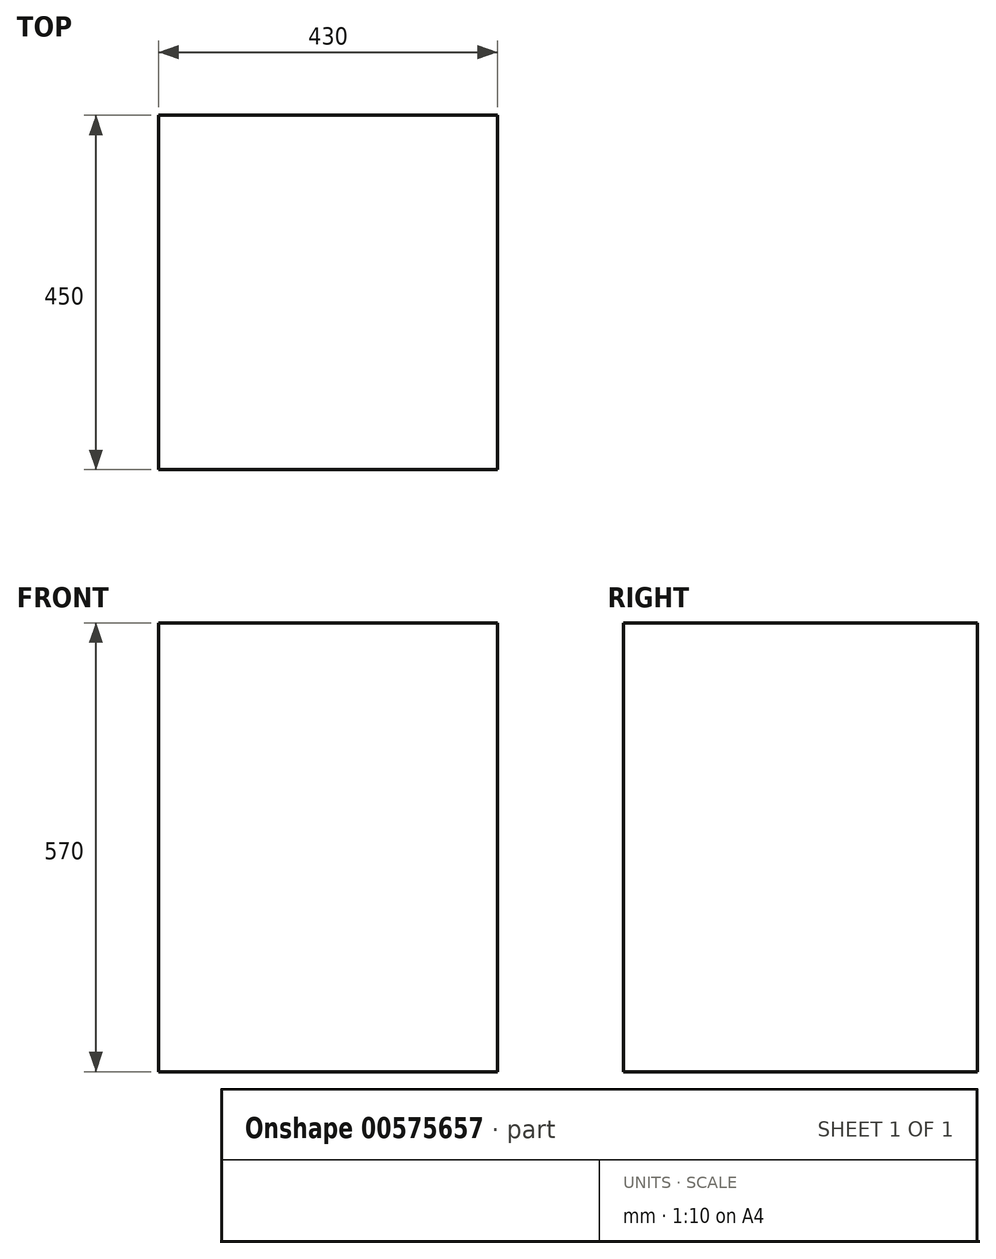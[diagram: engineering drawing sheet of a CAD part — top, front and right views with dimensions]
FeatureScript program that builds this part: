
annotation { "Feature Type Name" : "Feature", "Feature Type Description" : "" }
export const myFeature = defineFeature(function(context is Context, id is Id, definition is map)
    precondition{}
    {
        {
            var Q0;
            Q0=qCreatedBy(makeId("Top.planeOp"),FACE);
            var sketch = newSketch(context, id + "F0", { "sketchPlane" : qUnion([Q0])});
            skLineSegment(sketch, "E0.bottom", {"start": v(0, 0) * mm, "end": v(-430, 0) * mm});
            skLineSegment(sketch, "E0.top", {"start": v(0, 450) * mm, "end": v(-430, 450) * mm});
            skLineSegment(sketch, "E0.left", {"start": v(0, 0) * mm, "end": v(0, 450) * mm});
            skLineSegment(sketch, "E0.right", {"start": v(-430, 0) * mm, "end": v(-430, 450) * mm});
            skSolve(sketch);
        }
        {
            var Q0;
            Q0 = qSketchRegion(id + "F0", true);
            extrude(context, id + "F1", {"entities" : qUnion([Q0]), "depth" : (190 * 3) * mm, "offsetDistance" : 25 * mm});
        }
    });
